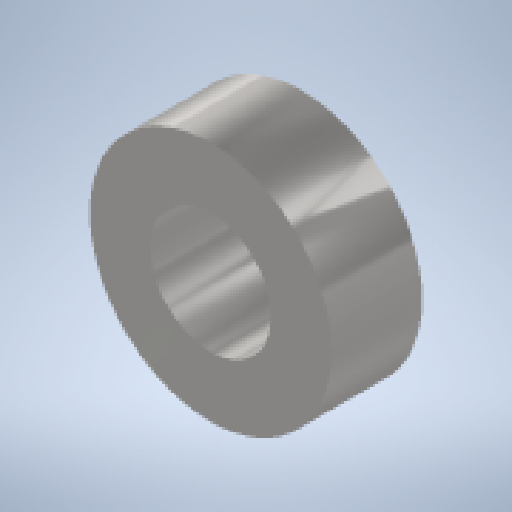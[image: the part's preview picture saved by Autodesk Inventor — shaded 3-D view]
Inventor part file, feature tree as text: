
AUTODESK INVENTOR PART (.ipt)
format: ipt  version: 2024 (Build 280153000, 153)  size: 139,264 bytes
history: native  units: mm
features: other x1, extrude x1, sketch x1
ambient origin geometry x8: Origin, YZ Plane, XZ Plane, XY Plane, X Axis, Y Axis, Z Axis, Center Point
bodies: Body1 (feature_tree)
feature tree (3):
  other  "ソリッド1"
  extrude  "押し出し1"  Depth=4.0mm
  sketch  "スケッチ1"
